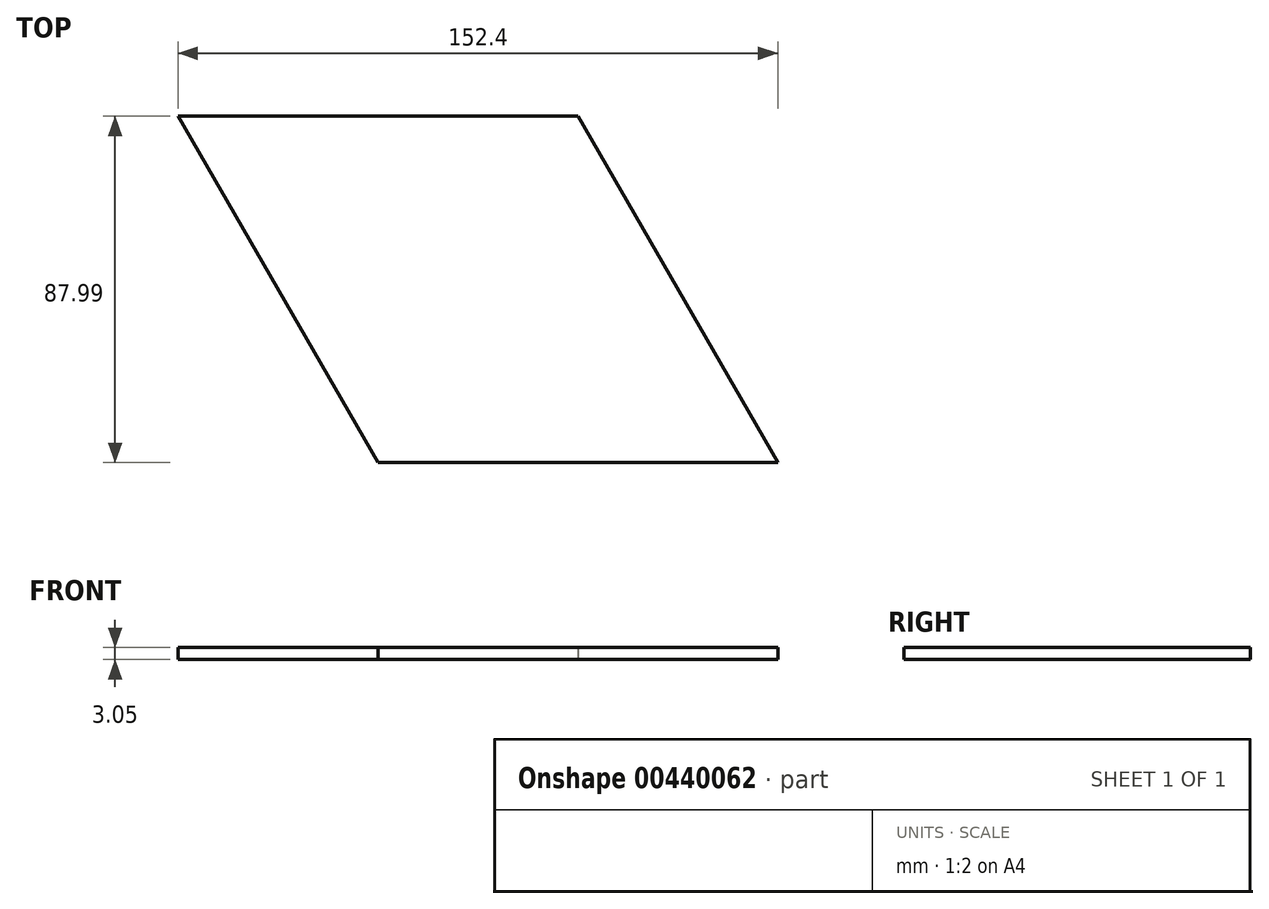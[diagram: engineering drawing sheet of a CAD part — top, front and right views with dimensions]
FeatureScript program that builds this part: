
annotation { "Feature Type Name" : "Feature", "Feature Type Description" : "" }
export const myFeature = defineFeature(function(context is Context, id is Id, definition is map)
    precondition{}
    {
        {
            var Q0;
            Q0=qCreatedBy(makeId("Top.planeOp"),FACE);
            var sketch = newSketch(context, id + "F0", { "sketchPlane" : qUnion([Q0])});
            skLineSegment(sketch, "E0", {"start": v(-101.6, -87.99) * mm, "end": v(-152.4, 0) * mm});
            skLineSegment(sketch, "E1", {"start": v(-50.8, 0) * mm, "end": v(-152.4, 0) * mm});
            skLineSegment(sketch, "E2.MirrorCS", {"start": v(-101.6, -87.99) * mm, "end": v(0, -87.99) * mm});
            skLineSegment(sketch, "E3.MirrorCS", {"start": v(-50.8, 0) * mm, "end": v(0, -87.99) * mm});
            skSolve(sketch);
        }
        {
            var Q0;
            Q0=makeQuery(id+"F0.imprint","IMPRINT",FACE,{"disambiguationData":[TD([[makeQuery(id+"F0.imprint","IMPRINT",EDGE,{"derivedFrom":sQuery(id+"F0.wireOp",EDGE,"E0")}),-1.0]])]});
            extrude(context, id + "F1", {"entities" : qUnion([Q0]), "depth" : 3.05 * mm});
        }
    });
